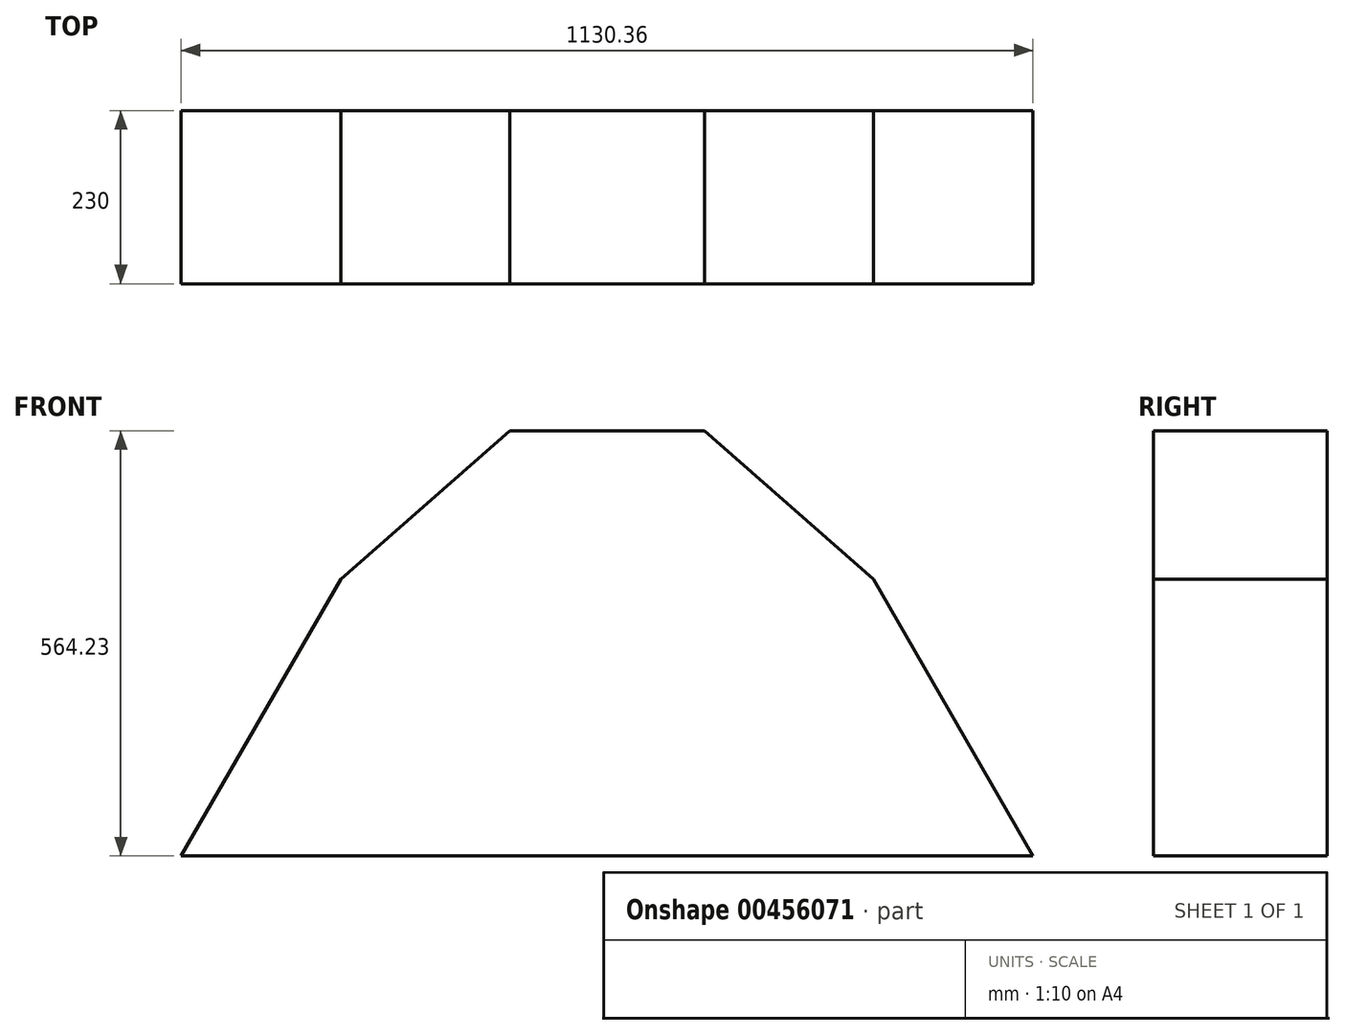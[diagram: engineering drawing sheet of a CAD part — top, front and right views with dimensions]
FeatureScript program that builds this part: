
annotation { "Feature Type Name" : "Feature", "Feature Type Description" : "" }
export const myFeature = defineFeature(function(context is Context, id is Id, definition is map)
    precondition{}
    {
        {
            var Q0;
            Q0=qCreatedBy(makeId("Front.planeOp"),FACE);
            var sketch = newSketch(context, id + "F0", { "sketchPlane" : qUnion([Q0])});
            skLineSegment(sketch, "E0.0", {"start": v(353.17, 40.9) * mm, "end": v(565.18, -326.3) * mm});
            skLineSegment(sketch, "E0.1", {"start": v(565.18, -326.3) * mm, "end": v(-565.18, -326.3) * mm});
            skLineSegment(sketch, "E0.2", {"start": v(-565.18, -326.3) * mm, "end": v(-353.17, 40.9) * mm});
            skLineSegment(sketch, "E1", {"start": v(-129.4, 237.92) * mm, "end": v(129.4, 237.92) * mm});
            skLineSegment(sketch, "E2", {"start": v(-129.4, 237.92) * mm, "end": v(-353.17, 40.9) * mm});
            skLineSegment(sketch, "E3.MirrorCS", {"start": v(129.4, 237.92) * mm, "end": v(353.17, 40.9) * mm});
            skPoint(sketch, "E4.orphan", {"position": v(0, 652.61) * mm});
            skSolve(sketch);
        }
        {
            var Q0;
            Q0=makeQuery(id+"F0.imprint","IMPRINT",FACE,{"disambiguationData":[TD([[makeQuery(id+"F0.imprint","IMPRINT",EDGE,{"derivedFrom":sQuery(id+"F0.wireOp",EDGE,"E0.0")}),-1.0]])]});
            extrude(context, id + "F1", {"entities" : qUnion([Q0]), "depth" : 230 * mm});
        }
    });
